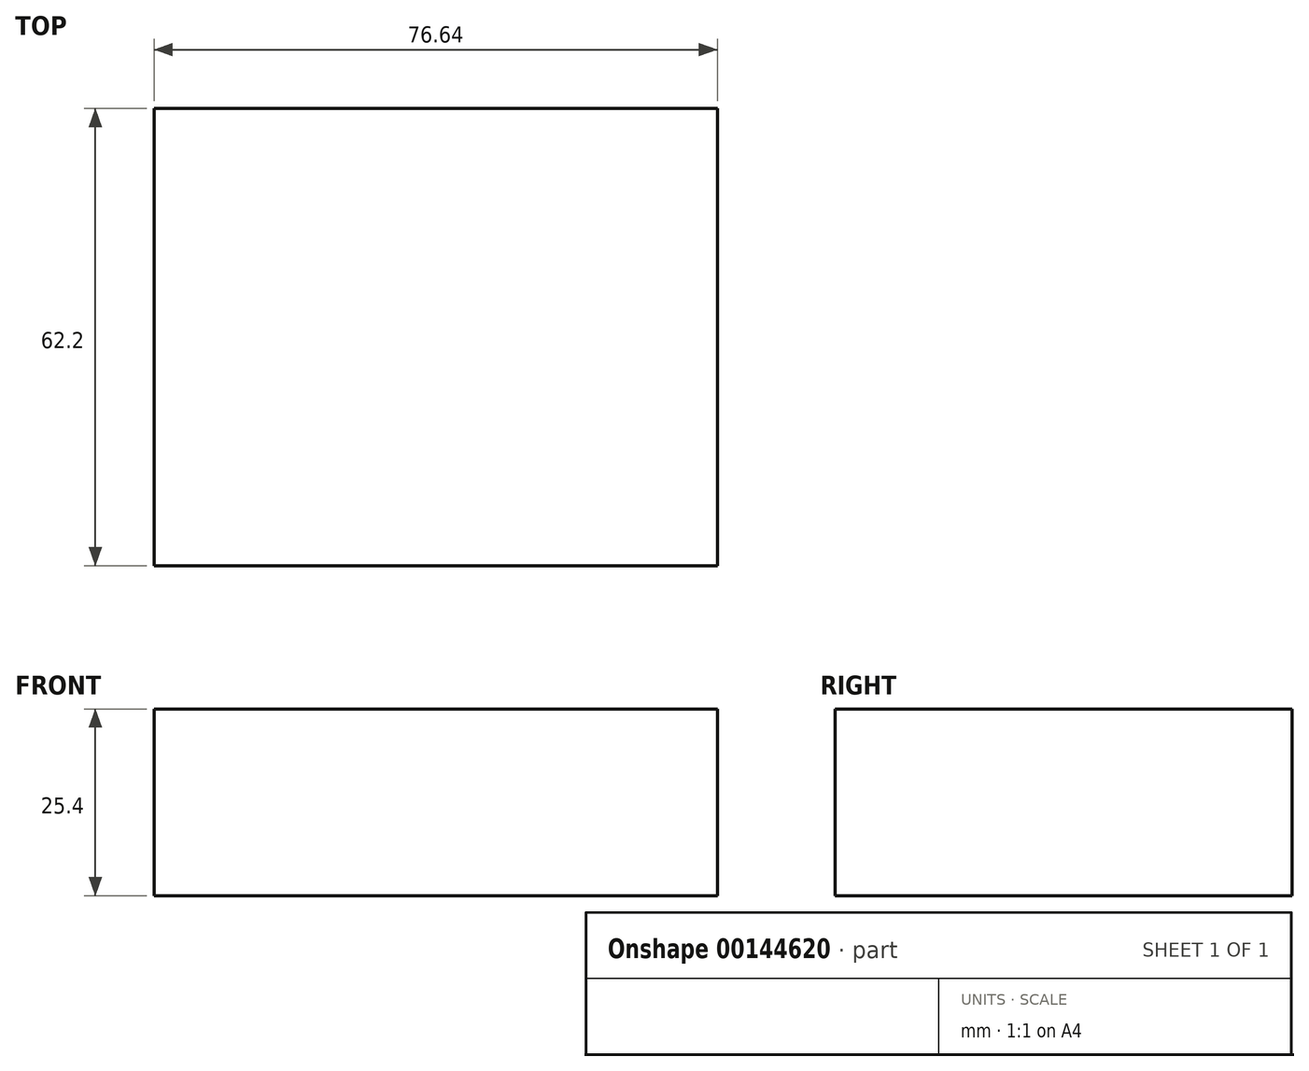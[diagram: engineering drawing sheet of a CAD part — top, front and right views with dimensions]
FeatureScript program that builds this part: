
annotation { "Feature Type Name" : "Feature", "Feature Type Description" : "" }
export const myFeature = defineFeature(function(context is Context, id is Id, definition is map)
    precondition{}
    {
        {
            var Q0;
            Q0=qCreatedBy(makeId("Top.planeOp"),FACE);
            var sketch = newSketch(context, id + "F0", { "sketchPlane" : qUnion([Q0])});
            skLineSegment(sketch, "E0.bottom", {"start": v(-36.22, -28.16) * mm, "end": v(40.42, -28.16) * mm});
            skLineSegment(sketch, "E0.top", {"start": v(-36.22, 34.04) * mm, "end": v(40.42, 34.04) * mm});
            skLineSegment(sketch, "E0.left", {"start": v(-36.22, -28.16) * mm, "end": v(-36.22, 34.04) * mm});
            skLineSegment(sketch, "E0.right", {"start": v(40.42, -28.16) * mm, "end": v(40.42, 34.04) * mm});
            skSolve(sketch);
        }
        {
            var Q0;
            Q0=makeQuery(id+"F0.imprint","IMPRINT",FACE,{"disambiguationData":[TD([[makeQuery(id+"F0.imprint","IMPRINT",EDGE,{"derivedFrom":sQuery(id+"F0.wireOp",EDGE,"E0.bottom")}),1.0]])]});
            extrude(context, id + "F1", {"entities" : qUnion([Q0]), "depth" : 25.4 * mm});
        }
    });
